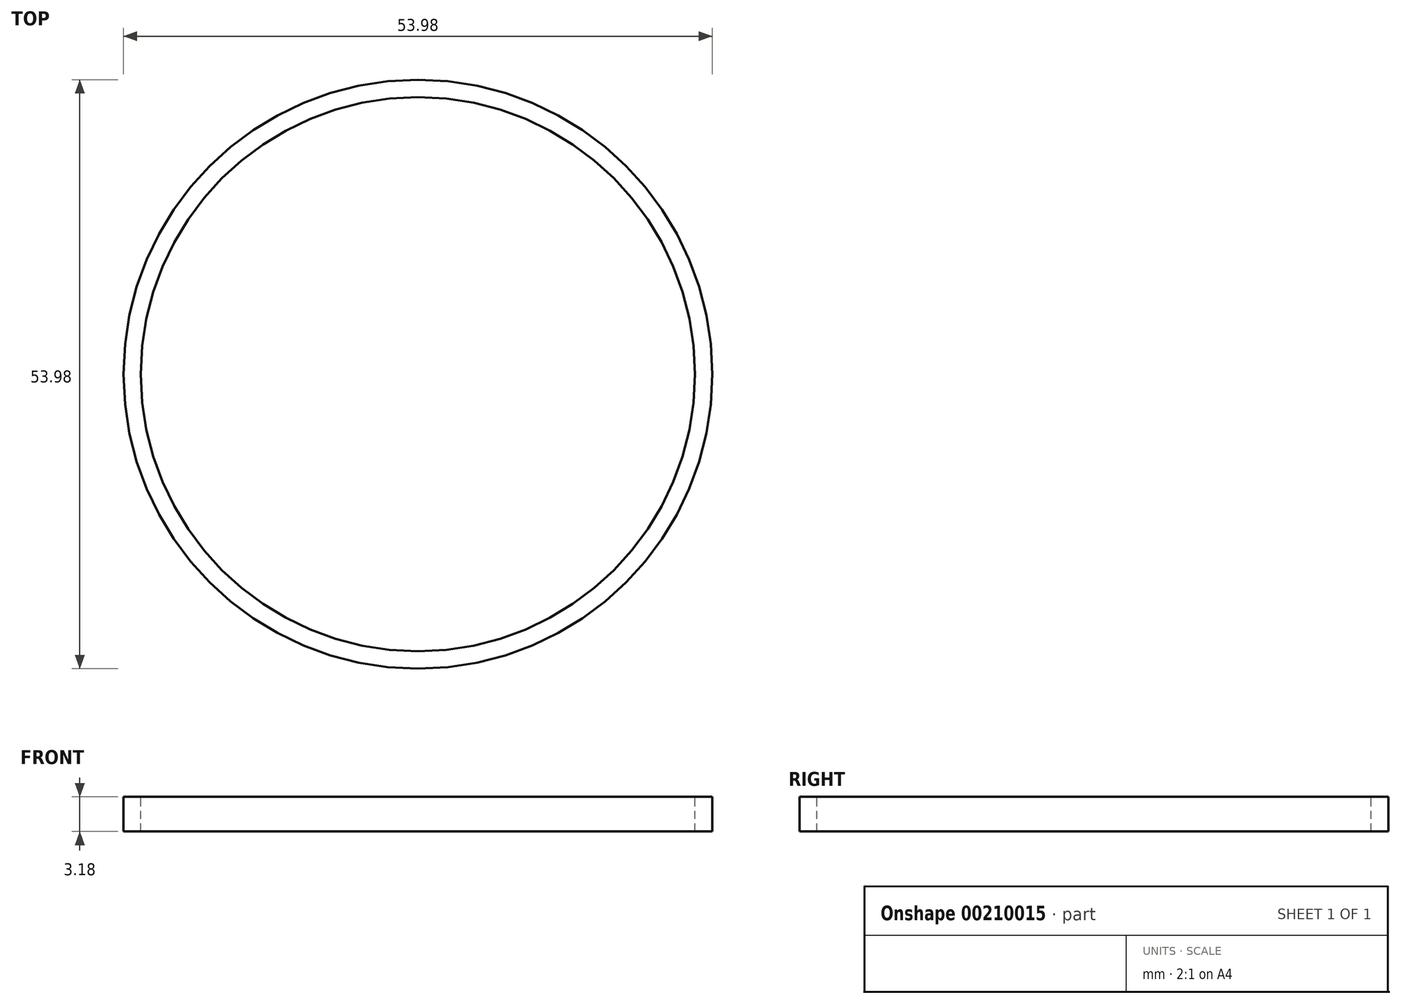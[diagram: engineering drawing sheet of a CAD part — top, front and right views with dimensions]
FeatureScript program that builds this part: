
annotation { "Feature Type Name" : "Feature", "Feature Type Description" : "" }
export const myFeature = defineFeature(function(context is Context, id is Id, definition is map)
    precondition{}
    {
        {
            var Q0;
            Q0=qCreatedBy(makeId("Top.planeOp"),FACE);
            var sketch = newSketch(context, id + "F0", { "sketchPlane" : qUnion([Q0])});
            skLineSegment(sketch, "E0.bottom", {"start": v(69.85, -44.45) * mm, "end": v(-69.85, -44.45) * mm});
            skLineSegment(sketch, "E0.top", {"start": v(69.85, 44.45) * mm, "end": v(-69.85, 44.45) * mm});
            skLineSegment(sketch, "E0.left", {"start": v(69.85, -44.45) * mm, "end": v(69.85, 44.45) * mm});
            skLineSegment(sketch, "E0.right", {"start": v(-69.85, -44.45) * mm, "end": v(-69.85, 44.45) * mm});
            skPoint(sketch, "E0.middle", {"position": v(0, 0) * mm});
            skCircle(sketch, "E1", {"center": v(0, 0) * mm, "radius": 25.4 * mm});
            skCircle(sketch, "E2", {"center": v(0, 0) * mm, "radius": 26.99 * mm});
            skSolve(sketch);
        }
        {
            var Q0;
            Q0=sQuery(id+"F0.wireOp",EDGE,"E1");
            var Q1;
            Q1=sQuery(id+"F0.wireOp",EDGE,"E2");
            extrude(context, id + "F1", {"bodyType" : ToolBodyType.SURFACE, "surfaceEntities" : qUnion([Q0, Q1]), "depth" : 3.17 * mm});
        }
    });
